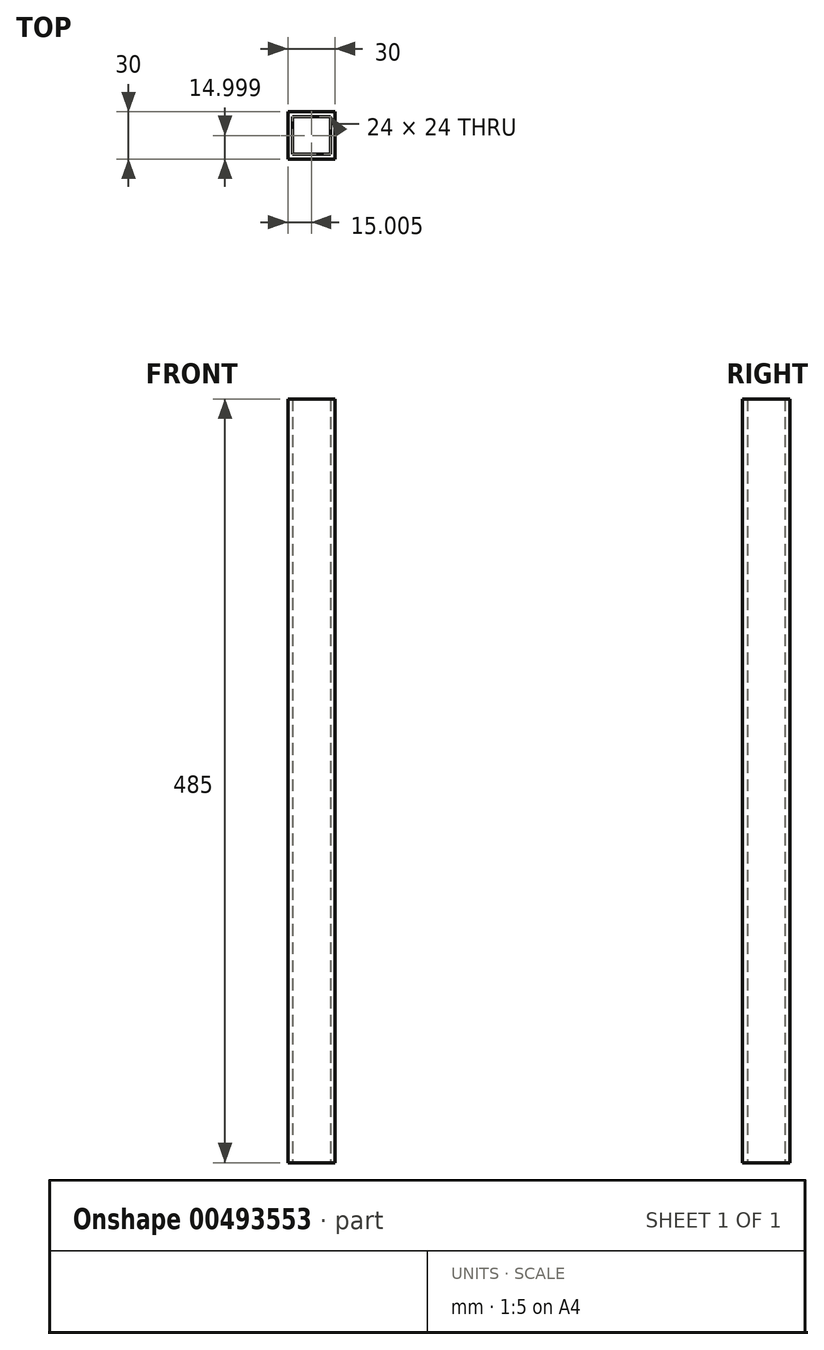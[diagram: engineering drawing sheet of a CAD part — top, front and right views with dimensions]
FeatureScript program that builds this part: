
annotation { "Feature Type Name" : "Feature", "Feature Type Description" : "" }
export const myFeature = defineFeature(function(context is Context, id is Id, definition is map)
    precondition{}
    {
        {
            var Q0;
            Q0=qCreatedBy(makeId("Top.planeOp"),FACE);
            var sketch = newSketch(context, id + "F0", { "sketchPlane" : qUnion([Q0])});
            skLineSegment(sketch, "E0.bottom", {"start": v(-9.06, 11.45) * mm, "end": v(14.94, 11.45) * mm});
            skLineSegment(sketch, "E0.top", {"start": v(-9.06, -12.55) * mm, "end": v(14.94, -12.55) * mm});
            skLineSegment(sketch, "E0.left", {"start": v(-9.06, 11.45) * mm, "end": v(-9.06, -12.55) * mm});
            skLineSegment(sketch, "E0.right", {"start": v(14.94, 11.45) * mm, "end": v(14.94, -12.55) * mm});
            skLineSegment(sketch, "E1.bottom", {"start": v(-12.06, 14.45) * mm, "end": v(17.94, 14.45) * mm});
            skLineSegment(sketch, "E1.top", {"start": v(-12.06, -15.55) * mm, "end": v(17.94, -15.55) * mm});
            skLineSegment(sketch, "E1.left", {"start": v(-12.06, 14.45) * mm, "end": v(-12.06, -15.55) * mm});
            skLineSegment(sketch, "E1.right", {"start": v(17.94, 14.45) * mm, "end": v(17.94, -15.55) * mm});
            skSolve(sketch);
        }
        {
            var Q0;
            Q0 = qSketchRegion(id + "F0", true);
            extrude(context, id + "F1", {"entities" : qUnion([Q0]), "depth" : 485 * mm});
        }
    });
